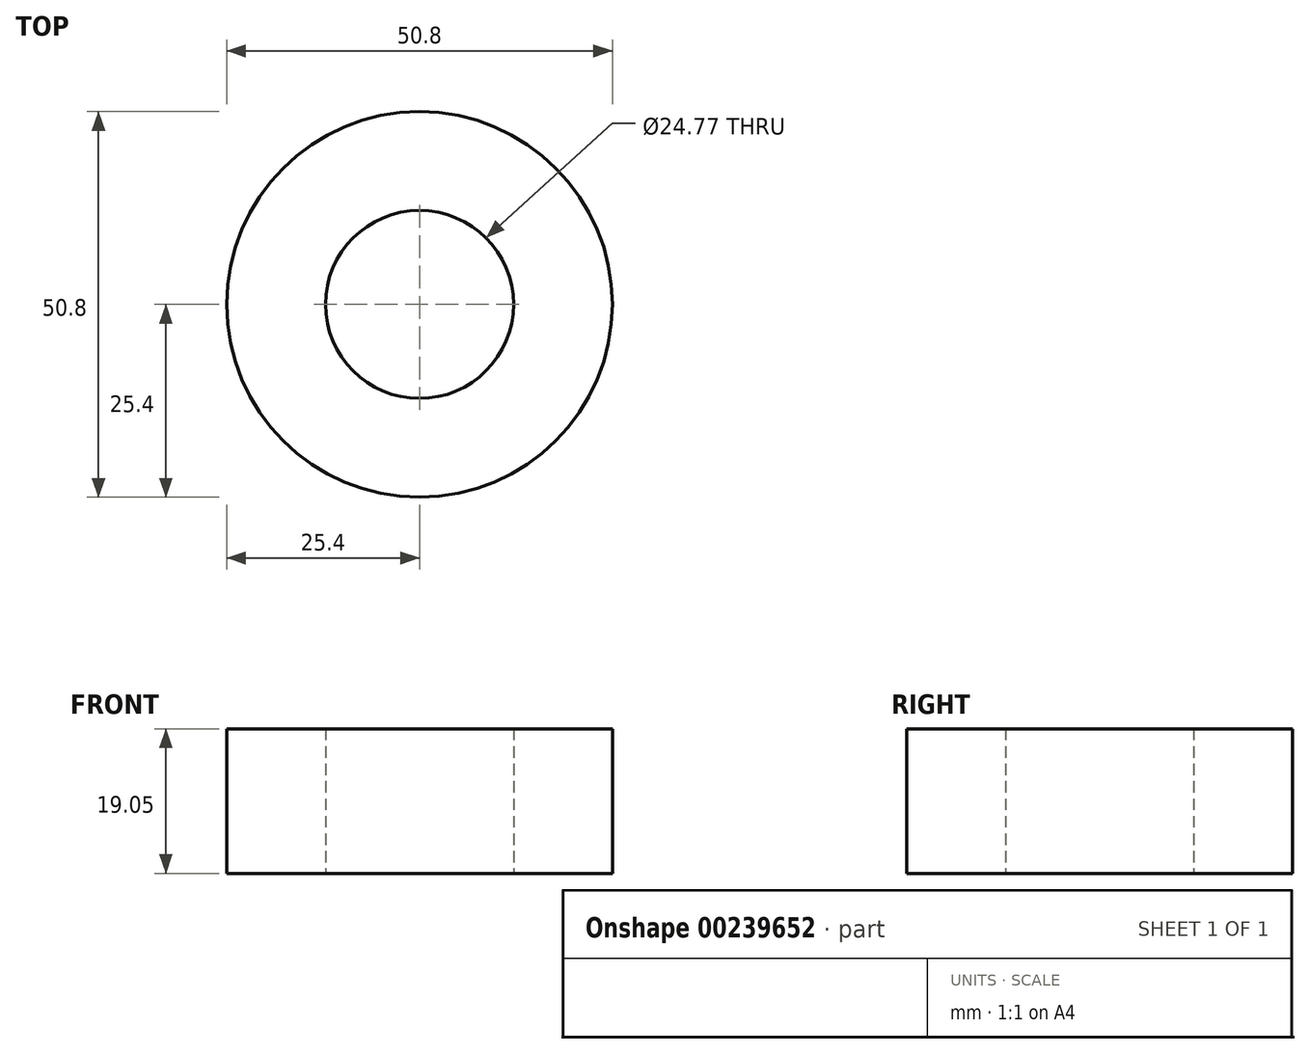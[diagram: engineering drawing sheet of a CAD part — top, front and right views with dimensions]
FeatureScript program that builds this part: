
annotation { "Feature Type Name" : "Feature", "Feature Type Description" : "" }
export const myFeature = defineFeature(function(context is Context, id is Id, definition is map)
    precondition{}
    {
        {
            var Q0;
            Q0=qCreatedBy(makeId("Top.planeOp"),FACE);
            var sketch = newSketch(context, id + "F0", { "sketchPlane" : qUnion([Q0])});
            skCircle(sketch, "E0", {"center": v(0, 0) * mm, "radius": 25.4 * mm});
            skCircle(sketch, "E1", {"center": v(0, 0) * mm, "radius": 17.46 * mm});
            skSolve(sketch);
        }
        {
            var Q0;
            Q0 = qSketchRegion(id + "F0", true);
            extrude(context, id + "F1", {"entities" : qUnion([Q0]), "depth" : 19.05 * mm});
        }
        {
            var Q0;
            Q0=qCreatedBy(makeId("Top.planeOp"),FACE);
            var sketch = newSketch(context, id + "F2", { "sketchPlane" : qUnion([Q0])});
            skCircle(sketch, "E2.0", {"center": v(0, 0) * mm, "radius": 17.46 * mm});
            skCircle(sketch, "E3.0", {"center": v(0, 0) * mm, "radius": 12.38 * mm});
            skSolve(sketch);
        }
        {
            var Q0;
            Q0=makeQuery(id+"F2.imprint","IMPRINT",FACE,{"disambiguationData":[TD([[makeQuery(id+"F2.imprint","IMPRINT",EDGE,{"derivedFrom":sQuery(id+"F2.wireOp",EDGE,"E2.0")}),1.0]])]});
            extrude(context, id + "F3", {"entities" : qUnion([Q0]), "operationType" : NewBodyOperationType.ADD, "depth" : 19.05 * mm});
        }
    });
